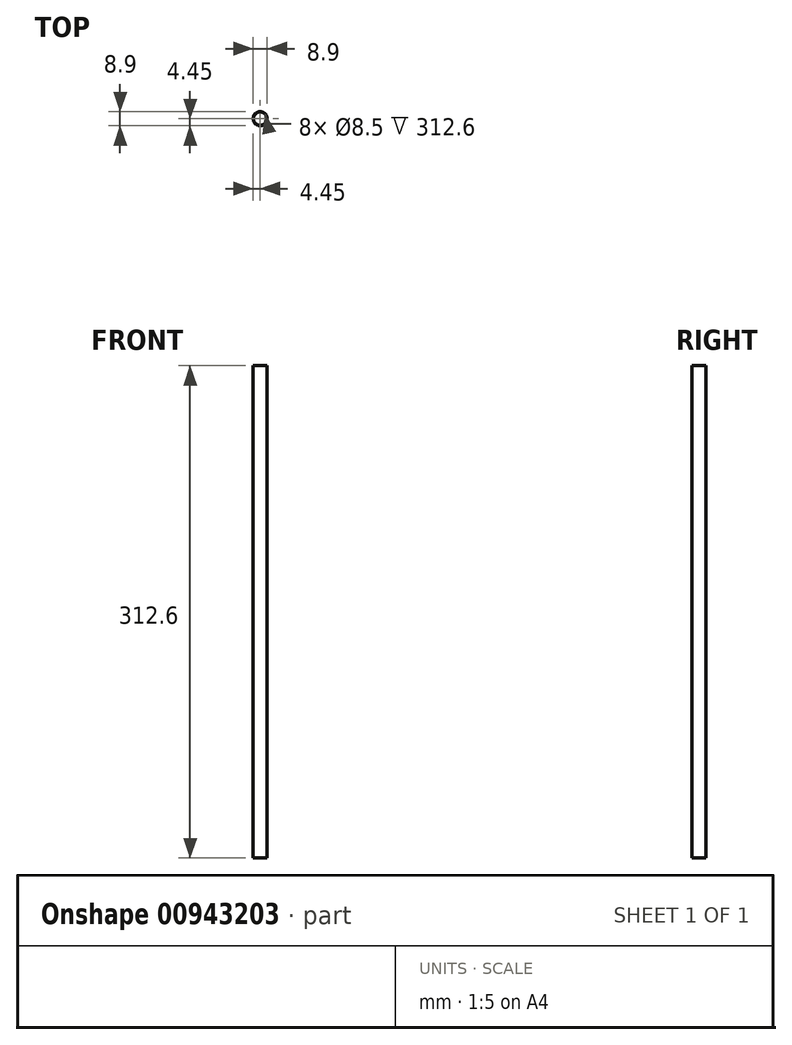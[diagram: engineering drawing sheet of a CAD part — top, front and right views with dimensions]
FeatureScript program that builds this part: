
annotation { "Feature Type Name" : "Feature", "Feature Type Description" : "" }
export const myFeature = defineFeature(function(context is Context, id is Id, definition is map)
    precondition{}
    {
        {
            var Q0;
            Q0=qCreatedBy(makeId("Top.planeOp"),FACE);
            var sketch = newSketch(context, id + "F0", { "sketchPlane" : qUnion([Q0])});
            skCircle(sketch, "E0", {"center": v(0, 0) * mm, "radius": 4.25 * mm});
            skCircle(sketch, "E1", {"center": v(0, 0) * mm, "radius": 4.45 * mm});
            skSolve(sketch);
        }
        {
            var Q0;
            Q0=qSketchRegion(id+"F0",true);
            extrude(context, id + "F1", {"entities" : qUnion([Q0]), "depth" : 312.6 * mm, "offsetDistance" : 25 * mm});
        }
    });
